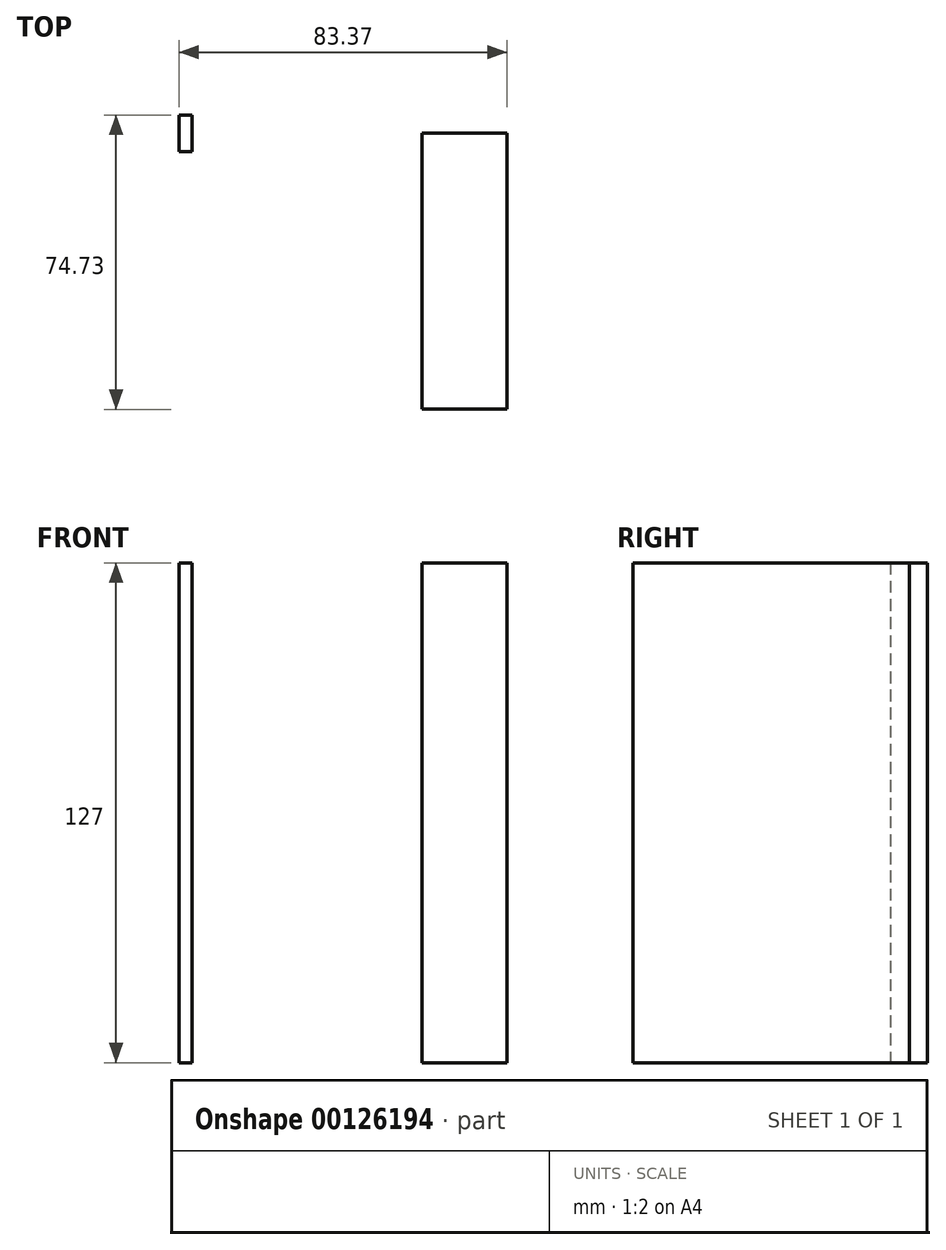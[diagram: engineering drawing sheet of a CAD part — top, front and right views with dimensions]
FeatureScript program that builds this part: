
annotation { "Feature Type Name" : "Feature", "Feature Type Description" : "" }
export const myFeature = defineFeature(function(context is Context, id is Id, definition is map)
    precondition{}
    {
        {
            var Q0;
            Q0=qCreatedBy(makeId("Top.planeOp"),FACE);
            var sketch = newSketch(context, id + "F0", { "sketchPlane" : qUnion([Q0])});
            skLineSegment(sketch, "E0.bottom", {"start": v(-29.94, 33.25) * mm, "end": v(-26.64, 33.25) * mm});
            skLineSegment(sketch, "E0.top", {"start": v(-29.94, 42.56) * mm, "end": v(-26.64, 42.56) * mm});
            skLineSegment(sketch, "E0.left", {"start": v(-29.94, 33.25) * mm, "end": v(-29.94, 42.56) * mm});
            skLineSegment(sketch, "E0.right", {"start": v(-26.64, 33.25) * mm, "end": v(-26.64, 42.56) * mm});
            skLineSegment(sketch, "E1.bottom", {"start": v(31.75, 38.03) * mm, "end": v(53.43, 38.03) * mm});
            skLineSegment(sketch, "E1.top", {"start": v(31.75, -32.17) * mm, "end": v(53.43, -32.17) * mm});
            skLineSegment(sketch, "E1.left", {"start": v(31.75, 38.03) * mm, "end": v(31.75, -32.17) * mm});
            skLineSegment(sketch, "E1.right", {"start": v(53.43, 38.03) * mm, "end": v(53.43, -32.17) * mm});
            skSolve(sketch);
        }
        {
            var Q0;
            Q0 = qSketchRegion(id + "F0", true);
            extrude(context, id + "F1", {"entities" : qUnion([Q0]), "depth" : 127 * mm});
        }
    });
